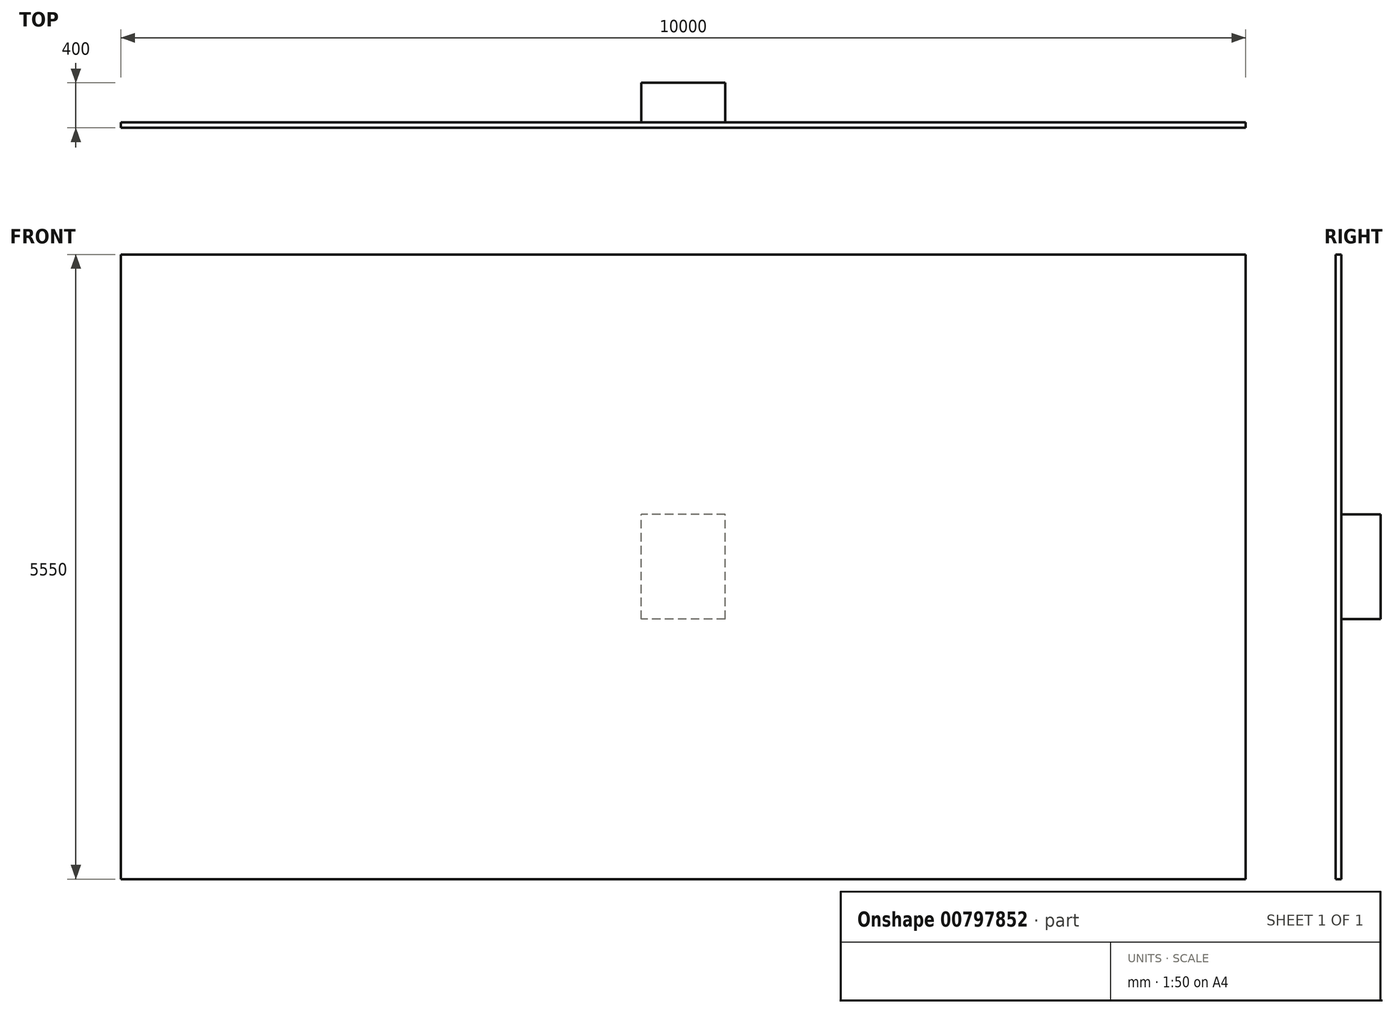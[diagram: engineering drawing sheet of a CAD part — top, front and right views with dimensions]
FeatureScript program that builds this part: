
annotation { "Feature Type Name" : "Feature", "Feature Type Description" : "" }
export const myFeature = defineFeature(function(context is Context, id is Id, definition is map)
    precondition{}
    {
        {
            var Q0;
            Q0=qCreatedBy(makeId("Front.planeOp"),FACE);
            var sketch = newSketch(context, id + "F0", { "sketchPlane" : qUnion([Q0])});
            skLineSegment(sketch, "E0.bottom", {"start": v(5000, -2775) * mm, "end": v(-5000, -2775) * mm});
            skLineSegment(sketch, "E0.top", {"start": v(5000, 2775) * mm, "end": v(-5000, 2775) * mm});
            skLineSegment(sketch, "E0.left", {"start": v(5000, -2775) * mm, "end": v(5000, 2775) * mm});
            skLineSegment(sketch, "E0.right", {"start": v(-5000, -2775) * mm, "end": v(-5000, 2775) * mm});
            skPoint(sketch, "E0.middle", {"position": v(0, 0) * mm});
            skSolve(sketch);
        }
        {
            var Q0;
            Q0 = qSketchRegion(id + "F0", true);
            extrude(context, id + "F1", {"entities" : qUnion([Q0]), "depth" : 50 * mm, "offsetDistance" : 25 * mm});
        }
        {
            var Q0;
            Q0=makeQuery(id+"F1.opExtrude","CAP_FACE",FACE,{"disambiguationData":[OSD([sQuery(id+"F0.wireOp",EDGE,"E0.bottom"),sQuery(id+"F0.wireOp",EDGE,"E0.top"),sQuery(id+"F0.wireOp",EDGE,"E0.left"),sQuery(id+"F0.wireOp",EDGE,"E0.right")])],"isStart":true});
            var sketch = newSketch(context, id + "F2", { "sketchPlane" : qUnion([Q0])});
            skLineSegment(sketch, "E1.bottom", {"start": v(-372.36, -464.88) * mm, "end": v(372.36, -464.88) * mm});
            skLineSegment(sketch, "E1.top", {"start": v(-372.36, 464.88) * mm, "end": v(372.36, 464.88) * mm});
            skLineSegment(sketch, "E1.left", {"start": v(-372.36, -464.88) * mm, "end": v(-372.36, 464.88) * mm});
            skLineSegment(sketch, "E1.right", {"start": v(372.36, -464.88) * mm, "end": v(372.36, 464.88) * mm});
            skPoint(sketch, "E1.middle", {"position": v(0, 0) * mm});
            skSolve(sketch);
        }
        {
            var Q0;
            Q0 = qSketchRegion(id + "F2", true);
            extrude(context, id + "F3", {"entities" : qUnion([Q0]), "operationType" : NewBodyOperationType.ADD, "depth" : 350 * mm, "offsetDistance" : 25 * mm});
        }
    });
